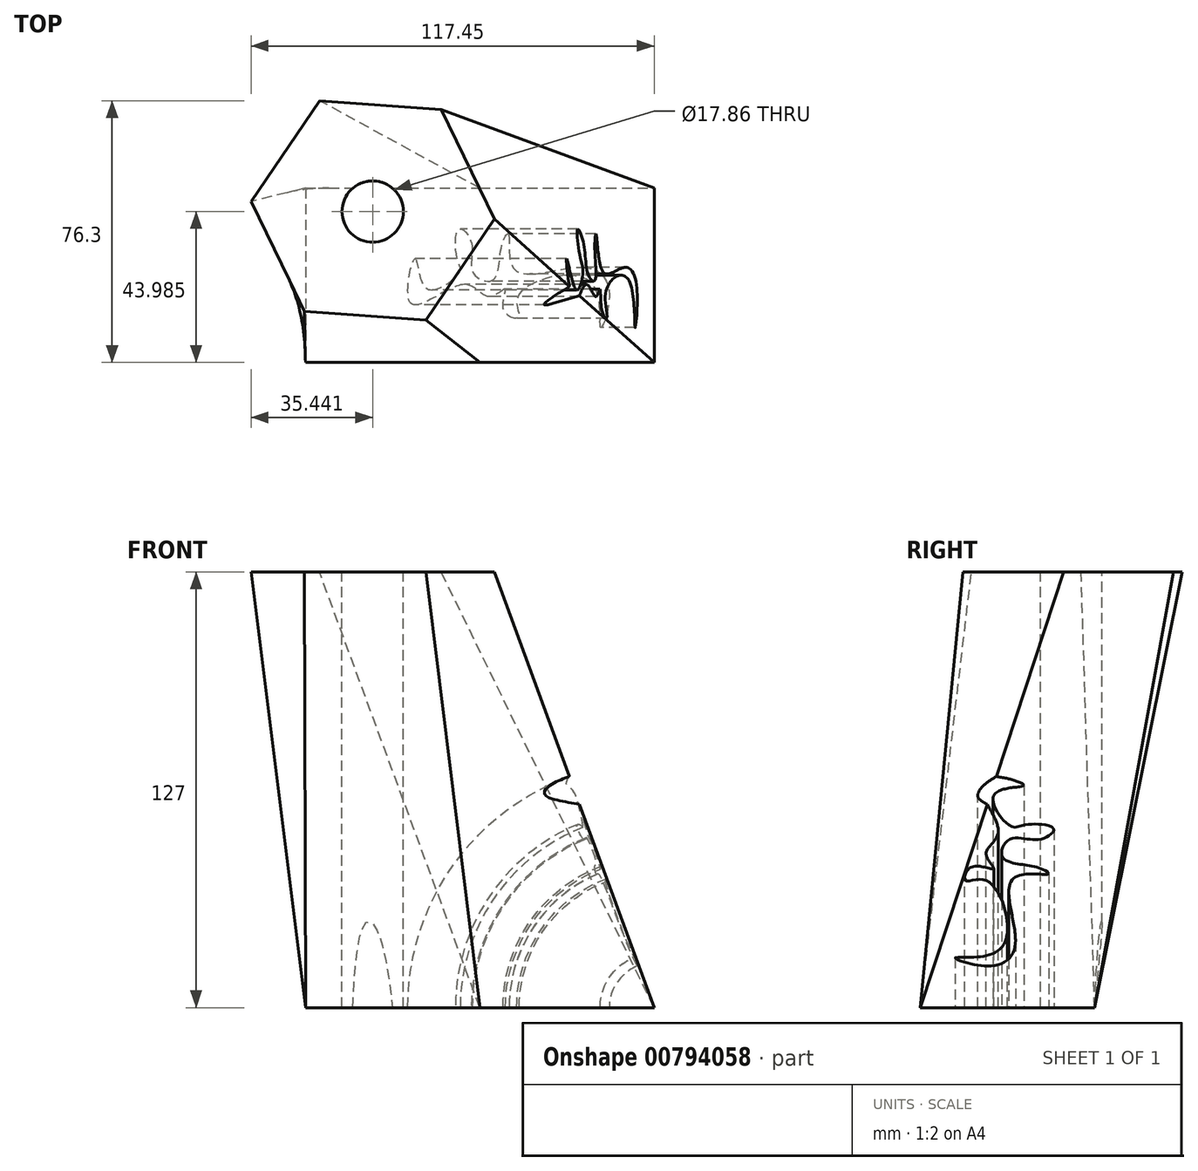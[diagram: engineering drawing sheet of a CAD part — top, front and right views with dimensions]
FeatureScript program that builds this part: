
annotation { "Feature Type Name" : "Feature", "Feature Type Description" : "" }
export const myFeature = defineFeature(function(context is Context, id is Id, definition is map)
    precondition{}
    {
        {
            var Q0;
            Q0=qCreatedBy(makeId("Top.planeOp"),FACE);
            var sketch = newSketch(context, id + "F0", { "sketchPlane" : qUnion([Q0])});
            skLineSegment(sketch, "E0.bottom", {"start": v(0, 0) * mm, "end": v(101.6, 0) * mm});
            skLineSegment(sketch, "E0.top", {"start": v(0, -50.8) * mm, "end": v(101.6, -50.8) * mm});
            skLineSegment(sketch, "E0.left", {"start": v(0, 0) * mm, "end": v(0, -50.8) * mm});
            skLineSegment(sketch, "E0.right", {"start": v(101.6, 0) * mm, "end": v(101.6, -50.8) * mm});
            skSolve(sketch);
        }
        {
            var Q0;
            Q0=qCreatedBy(makeId("Top.planeOp"),FACE);
            cPlane(context, id + "F1", {"entities" : qUnion([Q0]), "cplaneType" : CPlaneType.OFFSET, "offset" : 127 * mm, "width" : 152.4 * mm, "height" : 152.4 * mm});
        }
        {
            var Q0;
            Q0=qCreatedBy(id+"F1.planeOp",FACE);
            var sketch = newSketch(context, id + "F2", { "sketchPlane" : qUnion([Q0])});
            skCircle(sketch, "E1.cCircle", {"center": v(19.6, -6.47) * mm, "radius": 30.78 * mm, "construction": true});
            skLineSegment(sketch, "E1.0", {"start": v(55.04, -9.01) * mm, "end": v(35.12, -38.44) * mm});
            skLineSegment(sketch, "E1.1", {"start": v(35.12, -38.44) * mm, "end": v(-0.33, -35.9) * mm});
            skLineSegment(sketch, "E1.2", {"start": v(-0.33, -35.9) * mm, "end": v(-15.85, -3.93) * mm});
            skLineSegment(sketch, "E1.3", {"start": v(-15.85, -3.93) * mm, "end": v(4.07, 25.5) * mm});
            skLineSegment(sketch, "E1.4", {"start": v(4.07, 25.5) * mm, "end": v(39.52, 22.95) * mm});
            skLineSegment(sketch, "E1.5", {"start": v(39.52, 22.95) * mm, "end": v(55.04, -9.01) * mm});
            skPoint(sketch, "E1.0.midPoint", {"position": v(45.08, -23.73) * mm});
            skSolve(sketch);
        }
        {
            var Q0;
            Q0=makeQuery(id+"F0.imprint","IMPRINT",FACE,{"disambiguationData":[TD([[makeQuery(id+"F0.imprint","IMPRINT",EDGE,{"derivedFrom":sQuery(id+"F0.wireOp",EDGE,"E0.bottom")}),-1.0]])]});
            var Q1;
            Q1=makeQuery(id+"F2.imprint","IMPRINT",FACE,{"disambiguationData":[TD([[makeQuery(id+"F2.imprint","IMPRINT",EDGE,{"derivedFrom":sQuery(id+"F2.wireOp",EDGE,"E1.0")}),-1.0]])]});
            loft(context, id + "F3", {"sheetProfilesArray" : [{ "sheetProfileEntities" : qUnion([Q0]) }, { "sheetProfileEntities" : qUnion([Q1]) }]});
        }
        {
            var Q0;
            Q0=makeQuery(id+"F3.opLoft","CAP_FACE",FACE,{"disambiguationData":[OSD([makeQuery(id+"F2.imprint","IMPRINT",FACE,{"disambiguationData":[TD([[makeQuery(id+"F2.imprint","IMPRINT",EDGE,{"derivedFrom":sQuery(id+"F2.wireOp",EDGE,"E1.0")}),-1.0]])]})])],"isStart":true});
            var sketch = newSketch(context, id + "F4", { "sketchPlane" : qUnion([Q0])});
            skCircle(sketch, "E2", {"center": v(19.6, -6.81) * mm, "radius": 8.93 * mm});
            skSolve(sketch);
        }
        {
            var Q0;
            Q0=makeQuery(id+"F4.imprint","IMPRINT",FACE,{"disambiguationData":[TD([[makeQuery(id+"F4.imprint","IMPRINT",EDGE,{"derivedFrom":sQuery(id+"F4.wireOp",EDGE,"E2")}),1.0]])]});
            var Q1;
            Q1=sQuery(id+"F4.wireOp",EDGE,"E2");
            extrude(context, id + "F5", {"entities" : qUnion([Q0]), "operationType" : NewBodyOperationType.REMOVE, "surfaceEntities" : qUnion([Q1]), "endBound" : BoundingType.THROUGH_ALL, "oppositeDirection" : true, "depth" : 25.4 * mm, "offsetDistance" : 25.4 * mm});
        }
        {
            var Q0;
            Q0=makeQuery(id+"F3.opLoft","CAP_FACE",FACE,{"disambiguationData":[OSD([makeQuery(id+"F0.imprint","IMPRINT",FACE,{"disambiguationData":[TD([[makeQuery(id+"F0.imprint","IMPRINT",EDGE,{"derivedFrom":sQuery(id+"F0.wireOp",EDGE,"E0.bottom")}),-1.0]])]})])],"isStart":true});
            var sketch = newSketch(context, id + "F6", { "sketchPlane" : qUnion([Q0])});
            skFitSpline(sketch, "E3", {"points": [v(86, 40.62) * mm, v(83, 27.42) * mm, v(61.92, 31.53) * mm, v(62.13, 37.64) * mm, v(57.84, 35.7) * mm, v(58.18, 29.41) * mm, v(53.74, 31.62) * mm, v(46.18, 28.08) * mm, v(30.75, 33.56) * mm, v(31.89, 20.57) * mm, v(35.22, 29.15) * mm, v(44.75, 24.62) * mm, v(44.26, 20.59) * mm, v(44.75, 11.96) * mm, v(48.41, 16.06) * mm, v(48.84, 24.65) * mm, v(54.57, 26.77) * mm, v(57.2, 16.75) * mm, v(59.16, 13.44) * mm, v(60.88, 23.62) * mm, v(81.29, 23.1) * mm, v(88.53, 30.91) * mm, v(86, 40.62) * mm]});
            skSolve(sketch);
        }
        {
            var Q0;
            Q0=makeQuery(id+"F6.imprint","IMPRINT",FACE,{"disambiguationData":[TD([[makeQuery(id+"F6.imprint","IMPRINT",EDGE,{"derivedFrom":sQuery(id+"F6.wireOp",EDGE,"E3")}),1.0]])]});
            var Q1;
            Q1=makeQuery(id+"F3.opLoft","MID_CAP_EDGE",EDGE,{"disambiguationData":[OSD([sQuery(id+"F0.wireOp",EDGE,"E0.bottom"),sQuery(id+"F0.wireOp",EDGE,"E0.top"),sQuery(id+"F0.wireOp",EDGE,"E0.right")])],"capPos":0.0});
            revolve(context, id + "F7", {"operationType" : NewBodyOperationType.REMOVE, "surfaceOperationType" : NewSurfaceOperationType.NEW, "entities" : qUnion([Q0]), "axis" : qUnion([Q1]), "revolveType" : RevolveType.FULL, "oppositeDirection" : true});
        }
    });
